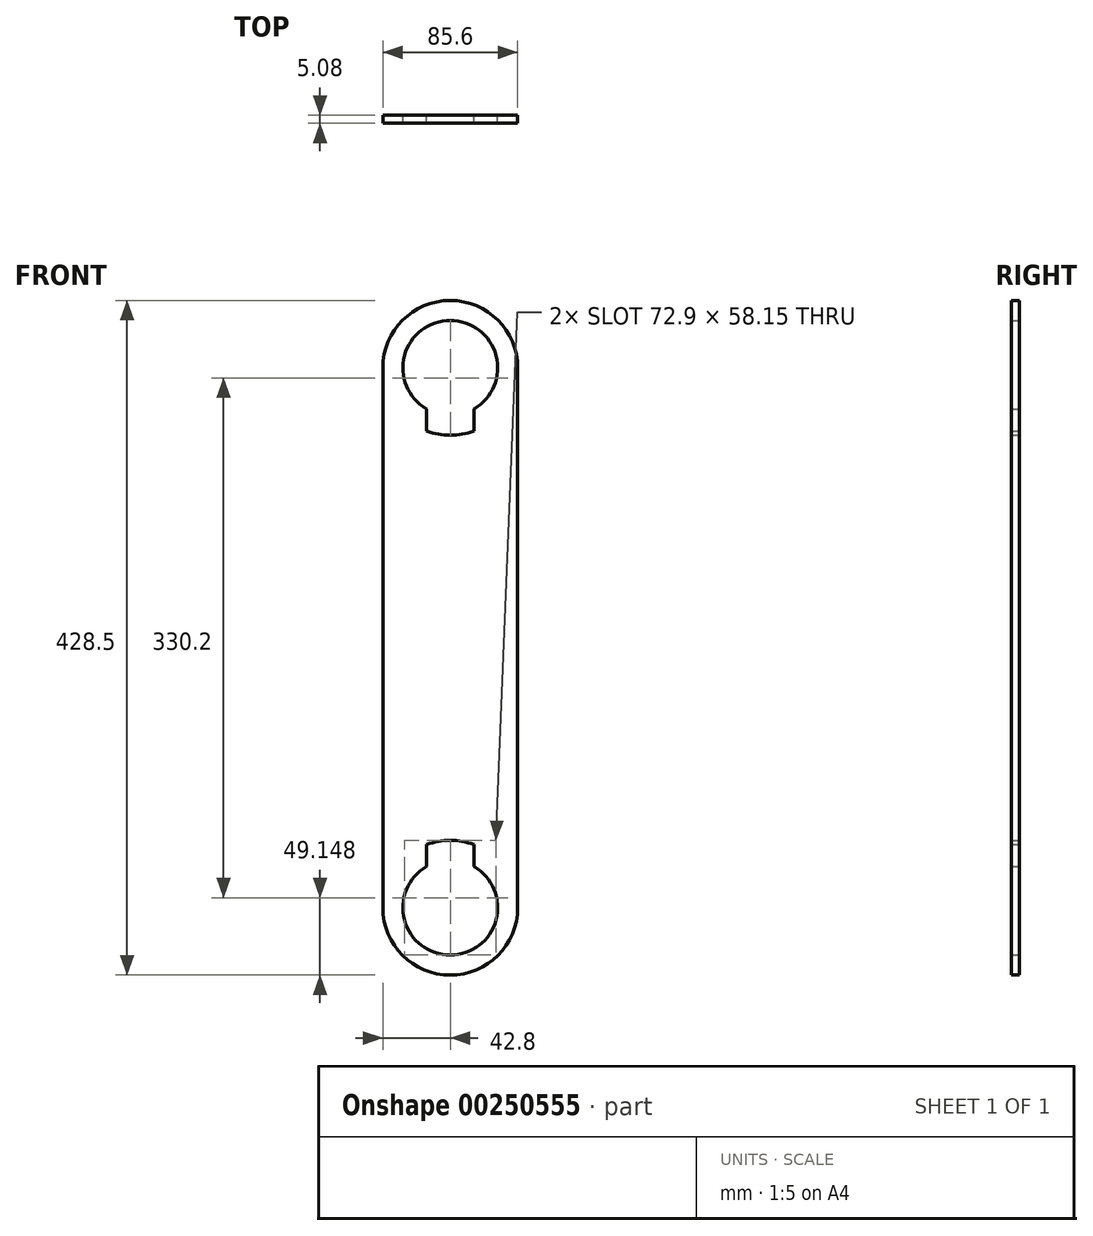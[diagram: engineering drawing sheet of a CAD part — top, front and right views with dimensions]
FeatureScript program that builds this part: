
annotation { "Feature Type Name" : "Feature", "Feature Type Description" : "" }
export const myFeature = defineFeature(function(context is Context, id is Id, definition is map)
    precondition{}
    {
        {
            var Q0;
            Q0=qCreatedBy(makeId("Front.planeOp"),FACE);
            var sketch = newSketch(context, id + "F0", { "sketchPlane" : qUnion([Q0])});
            skLineSegment(sketch, "E0", {"start": v(0, 164.64) * mm, "end": v(0, -178.26) * mm});
            skCircle(sketch, "E1", {"center": v(0, 164.64) * mm, "radius": 30.1 * mm});
            skCircle(sketch, "E2", {"center": v(0, -178.26) * mm, "radius": 30.1 * mm});
            skLineSegment(sketch, "E3", {"start": v(0, 194.74) * mm, "end": v(0, 207.44) * mm});
            skLineSegment(sketch, "E4", {"start": v(0, 164.64) * mm, "end": v(30.1, 164.64) * mm});
            skLineSegment(sketch, "E5", {"start": v(30.1, 164.64) * mm, "end": v(30.1, -178.26) * mm});
            skLineSegment(sketch, "E6", {"start": v(0, 164.64) * mm, "end": v(-30.1, 164.64) * mm});
            skLineSegment(sketch, "E7", {"start": v(-30.1, 164.64) * mm, "end": v(-30.1, -178.26) * mm});
            skLineSegment(sketch, "E8", {"start": v(-30.1, -178.26) * mm, "end": v(30.1, -178.26) * mm});
            skLineSegment(sketch, "E9", {"start": v(-30.1, 164.64) * mm, "end": v(-42.8, 164.64) * mm});
            skLineSegment(sketch, "E10", {"start": v(30.1, 164.64) * mm, "end": v(42.8, 164.64) * mm});
            skLineSegment(sketch, "E11", {"start": v(0, -178.26) * mm, "end": v(0, -208.36) * mm});
            skLineSegment(sketch, "E12", {"start": v(0, -208.36) * mm, "end": v(0, -221.06) * mm});
            skLineSegment(sketch, "E13", {"start": v(30.1, -178.26) * mm, "end": v(42.8, -178.26) * mm});
            skLineSegment(sketch, "E14", {"start": v(-30.1, -178.26) * mm, "end": v(-42.8, -178.26) * mm});
            skLineSegment(sketch, "E15", {"start": v(42.8, 164.64) * mm, "end": v(42.8, -178.26) * mm});
            skLineSegment(sketch, "E16", {"start": v(-42.8, 164.64) * mm, "end": v(-42.8, -178.26) * mm});
            skArc(sketch, "E17", {"start": v(42.8, 164.64) * mm, "mid": v(0, 207.44) * mm, "end": v(-42.8, 164.64) * mm});
            skArc(sketch, "E18", {"start": v(-42.8, -178.26) * mm, "mid": v(0, -221.06) * mm, "end": v(42.8, -178.26) * mm});
            skLineSegment(sketch, "E19", {"start": v(0, -148.16) * mm, "end": v(0, -135.46) * mm});
            skArc(sketch, "E20", {"start": v(42.8, -178.26) * mm, "mid": v(0, -135.46) * mm, "end": v(-42.8, -178.26) * mm});
            skLineSegment(sketch, "E21", {"start": v(0, 134.54) * mm, "end": v(0, 121.84) * mm});
            skArc(sketch, "E22", {"start": v(-42.8, 164.64) * mm, "mid": v(0, 121.84) * mm, "end": v(42.8, 164.64) * mm});
            skLineSegment(sketch, "E23", {"start": v(0, 164.64) * mm, "end": v(15.05, 164.64) * mm});
            skLineSegment(sketch, "E24", {"start": v(15.05, 164.64) * mm, "end": v(-15.05, 164.64) * mm});
            skLineSegment(sketch, "E25", {"start": v(-15.05, 164.64) * mm, "end": v(-15.05, -178.26) * mm});
            skLineSegment(sketch, "E26", {"start": v(15.05, 164.64) * mm, "end": v(15.05, -178.26) * mm});
            skLineSegment(sketch, "E27", {"start": v(42.8, 164.64) * mm, "end": v(42.8, 207.44) * mm});
            skLineSegment(sketch, "E28", {"start": v(42.8, -178.26) * mm, "end": v(42.8, -221.06) * mm});
            skSolve(sketch);
        }
        {
            var Q0;
            {var subQ2=sQuery(id+"F0.wireOp",EDGE,"E12");Q0=makeQuery(id+"F0.imprint","IMPRINT",FACE,{"disambiguationData":[TD([[makeQuery(id+"F0.imprint","IMPRINT",EDGE,{"derivedFrom":subQ2}),-1.0]])]});}
            var Q1;
            {var subQ2=sQuery(id+"F0.wireOp",EDGE,"E12");Q1=makeQuery(id+"F0.imprint","IMPRINT",FACE,{"disambiguationData":[TD([[makeQuery(id+"F0.imprint","IMPRINT",EDGE,{"derivedFrom":subQ2}),1.0]])]});}
            var Q2;
            {var subQ0=sQuery(id+"F0.wireOp",EDGE,"E10");Q2=makeQuery(id+"F0.imprint","IMPRINT",FACE,{"disambiguationData":[TD([[makeQuery(id+"F0.imprint","IMPRINT",EDGE,{"derivedFrom":subQ0}),-1.0]])]});}
            var Q3;
            {var subQ0=sQuery(id+"F0.wireOp",EDGE,"E13");Q3=makeQuery(id+"F0.imprint","IMPRINT",FACE,{"disambiguationData":[TD([[makeQuery(id+"F0.imprint","IMPRINT",EDGE,{"derivedFrom":subQ0}),1.0]])]});}
            var Q4;
            {var subQ0=sQuery(id+"F0.wireOp",EDGE,"E9");Q4=makeQuery(id+"F0.imprint","IMPRINT",FACE,{"disambiguationData":[TD([[makeQuery(id+"F0.imprint","IMPRINT",EDGE,{"derivedFrom":subQ0}),1.0]])]});}
            var Q5;
            {var subQ0=sQuery(id+"F0.wireOp",EDGE,"E14");Q5=makeQuery(id+"F0.imprint","IMPRINT",FACE,{"disambiguationData":[TD([[makeQuery(id+"F0.imprint","IMPRINT",EDGE,{"derivedFrom":subQ0}),-1.0]])]});}
            var Q6;
            {var subQ3=sQuery(id+"F0.wireOp",EDGE,"E19");Q6=makeQuery(id+"F0.imprint","IMPRINT",FACE,{"disambiguationData":[TD([[makeQuery(id+"F0.imprint","IMPRINT",EDGE,{"derivedFrom":subQ3}),-1.0]])]});}
            var Q7;
            {var subQ3=sQuery(id+"F0.wireOp",EDGE,"E19");Q7=makeQuery(id+"F0.imprint","IMPRINT",FACE,{"disambiguationData":[TD([[makeQuery(id+"F0.imprint","IMPRINT",EDGE,{"derivedFrom":subQ3}),1.0]])]});}
            var Q8;
            {var subQ3=sQuery(id+"F0.wireOp",EDGE,"E21");Q8=makeQuery(id+"F0.imprint","IMPRINT",FACE,{"disambiguationData":[TD([[makeQuery(id+"F0.imprint","IMPRINT",EDGE,{"derivedFrom":subQ3}),-1.0]])]});}
            var Q9;
            {var subQ3=sQuery(id+"F0.wireOp",EDGE,"E21");Q9=makeQuery(id+"F0.imprint","IMPRINT",FACE,{"disambiguationData":[TD([[makeQuery(id+"F0.imprint","IMPRINT",EDGE,{"derivedFrom":subQ3}),1.0]])]});}
            var Q10;
            {var subQ0=sQuery(id+"F0.wireOp",EDGE,"E5");var subQ5=sQuery(id+"F0.wireOp",EDGE,"E22");var subQ6=makeQuery(id+"F0.imprint","INTERSECT",VERTEX,{"derivedFrom":[subQ0,subQ5]});Q10=makeQuery(id+"F0.imprint","IMPRINT",FACE,{"disambiguationData":[TD([[makeQuery(id+"F0.imprint","IMPRINT",EDGE,{"disambiguationData":[TD([[subQ6,1.0]])],"derivedFrom":subQ5}),1.0]])]});}
            var Q11;
            {var subQ0=sQuery(id+"F0.wireOp",EDGE,"E5");var subQ5=sQuery(id+"F0.wireOp",EDGE,"E20");var subQ6=makeQuery(id+"F0.imprint","INTERSECT",VERTEX,{"derivedFrom":[subQ0,subQ5]});Q11=makeQuery(id+"F0.imprint","IMPRINT",FACE,{"disambiguationData":[TD([[makeQuery(id+"F0.imprint","IMPRINT",EDGE,{"disambiguationData":[TD([[subQ6,-1.0]])],"derivedFrom":subQ5}),1.0]])]});}
            var Q12;
            {var subQ0=sQuery(id+"F0.wireOp",EDGE,"E7");var subQ5=sQuery(id+"F0.wireOp",EDGE,"E20");var subQ6=makeQuery(id+"F0.imprint","INTERSECT",VERTEX,{"derivedFrom":[subQ0,subQ5]});Q12=makeQuery(id+"F0.imprint","IMPRINT",FACE,{"disambiguationData":[TD([[makeQuery(id+"F0.imprint","IMPRINT",EDGE,{"disambiguationData":[TD([[subQ6,1.0]])],"derivedFrom":subQ5}),1.0]])]});}
            var Q13;
            {var subQ0=sQuery(id+"F0.wireOp",EDGE,"E7");var subQ5=sQuery(id+"F0.wireOp",EDGE,"E22");var subQ6=makeQuery(id+"F0.imprint","INTERSECT",VERTEX,{"derivedFrom":[subQ0,subQ5]});Q13=makeQuery(id+"F0.imprint","IMPRINT",FACE,{"disambiguationData":[TD([[makeQuery(id+"F0.imprint","IMPRINT",EDGE,{"disambiguationData":[TD([[subQ6,-1.0]])],"derivedFrom":subQ5}),1.0]])]});}
            var Q14;
            {var subQ0=sQuery(id+"F0.wireOp",EDGE,"E3");Q14=makeQuery(id+"F0.imprint","IMPRINT",FACE,{"disambiguationData":[TD([[makeQuery(id+"F0.imprint","IMPRINT",EDGE,{"derivedFrom":subQ0}),1.0]])]});}
            var Q15;
            {var subQ0=sQuery(id+"F0.wireOp",EDGE,"E3");Q15=makeQuery(id+"F0.imprint","IMPRINT",FACE,{"disambiguationData":[TD([[makeQuery(id+"F0.imprint","IMPRINT",EDGE,{"derivedFrom":subQ0}),-1.0]])]});}
            var Q16;
            {var subQ5=sQuery(id+"F0.wireOp",EDGE,"E15");Q16=makeQuery(id+"F0.imprint","IMPRINT",FACE,{"disambiguationData":[TD([[makeQuery(id+"F0.imprint","IMPRINT",EDGE,{"derivedFrom":subQ5}),-1.0]])]});}
            var Q17;
            {var subQ5=sQuery(id+"F0.wireOp",EDGE,"E16");Q17=makeQuery(id+"F0.imprint","IMPRINT",FACE,{"disambiguationData":[TD([[makeQuery(id+"F0.imprint","IMPRINT",EDGE,{"derivedFrom":subQ5}),1.0]])]});}
            var Q18;
            {var subQ0=sQuery(id+"F0.wireOp",EDGE,"E20");var subQ5=sQuery(id+"F0.wireOp",EDGE,"E25");var subQ6=makeQuery(id+"F0.imprint","INTERSECT",VERTEX,{"derivedFrom":[subQ0,subQ5]});Q18=makeQuery(id+"F0.imprint","IMPRINT",FACE,{"disambiguationData":[TD([[makeQuery(id+"F0.imprint","IMPRINT",EDGE,{"disambiguationData":[TD([[subQ6,1.0]])],"derivedFrom":subQ5}),1.0]])]});}
            var Q19;
            {var subQ0=sQuery(id+"F0.wireOp",EDGE,"E20");var subQ5=sQuery(id+"F0.wireOp",EDGE,"E26");var subQ6=makeQuery(id+"F0.imprint","INTERSECT",VERTEX,{"derivedFrom":[subQ0,subQ5]});Q19=makeQuery(id+"F0.imprint","IMPRINT",FACE,{"disambiguationData":[TD([[makeQuery(id+"F0.imprint","IMPRINT",EDGE,{"disambiguationData":[TD([[subQ6,1.0]])],"derivedFrom":subQ5}),-1.0]])]});}
            var Q20;
            {var subQ0=sQuery(id+"F0.wireOp",EDGE,"E22");var subQ1=sQuery(id+"F0.wireOp",EDGE,"E5");var subQ2=makeQuery(id+"F0.imprint","INTERSECT",VERTEX,{"derivedFrom":[subQ1,subQ0]});Q20=makeQuery(id+"F0.imprint","IMPRINT",FACE,{"disambiguationData":[TD([[makeQuery(id+"F0.imprint","IMPRINT",EDGE,{"disambiguationData":[TD([[subQ2,-1.0]])],"derivedFrom":subQ1}),-1.0]])]});}
            var Q21;
            {var subQ0=sQuery(id+"F0.wireOp",EDGE,"E22");var subQ1=sQuery(id+"F0.wireOp",EDGE,"E7");var subQ2=makeQuery(id+"F0.imprint","INTERSECT",VERTEX,{"derivedFrom":[subQ1,subQ0]});Q21=makeQuery(id+"F0.imprint","IMPRINT",FACE,{"disambiguationData":[TD([[makeQuery(id+"F0.imprint","IMPRINT",EDGE,{"disambiguationData":[TD([[subQ2,-1.0]])],"derivedFrom":subQ1}),1.0]])]});}
            extrude(context, id + "F1", {"entities" : qUnion([Q0, Q1, Q2, Q3, Q4, Q5, Q6, Q7, Q8, Q9, Q10, Q11, Q12, Q13, Q14, Q15, Q16, Q17, Q18, Q19, Q20, Q21]), "depth" : 5.08 * mm});
        }
    });
